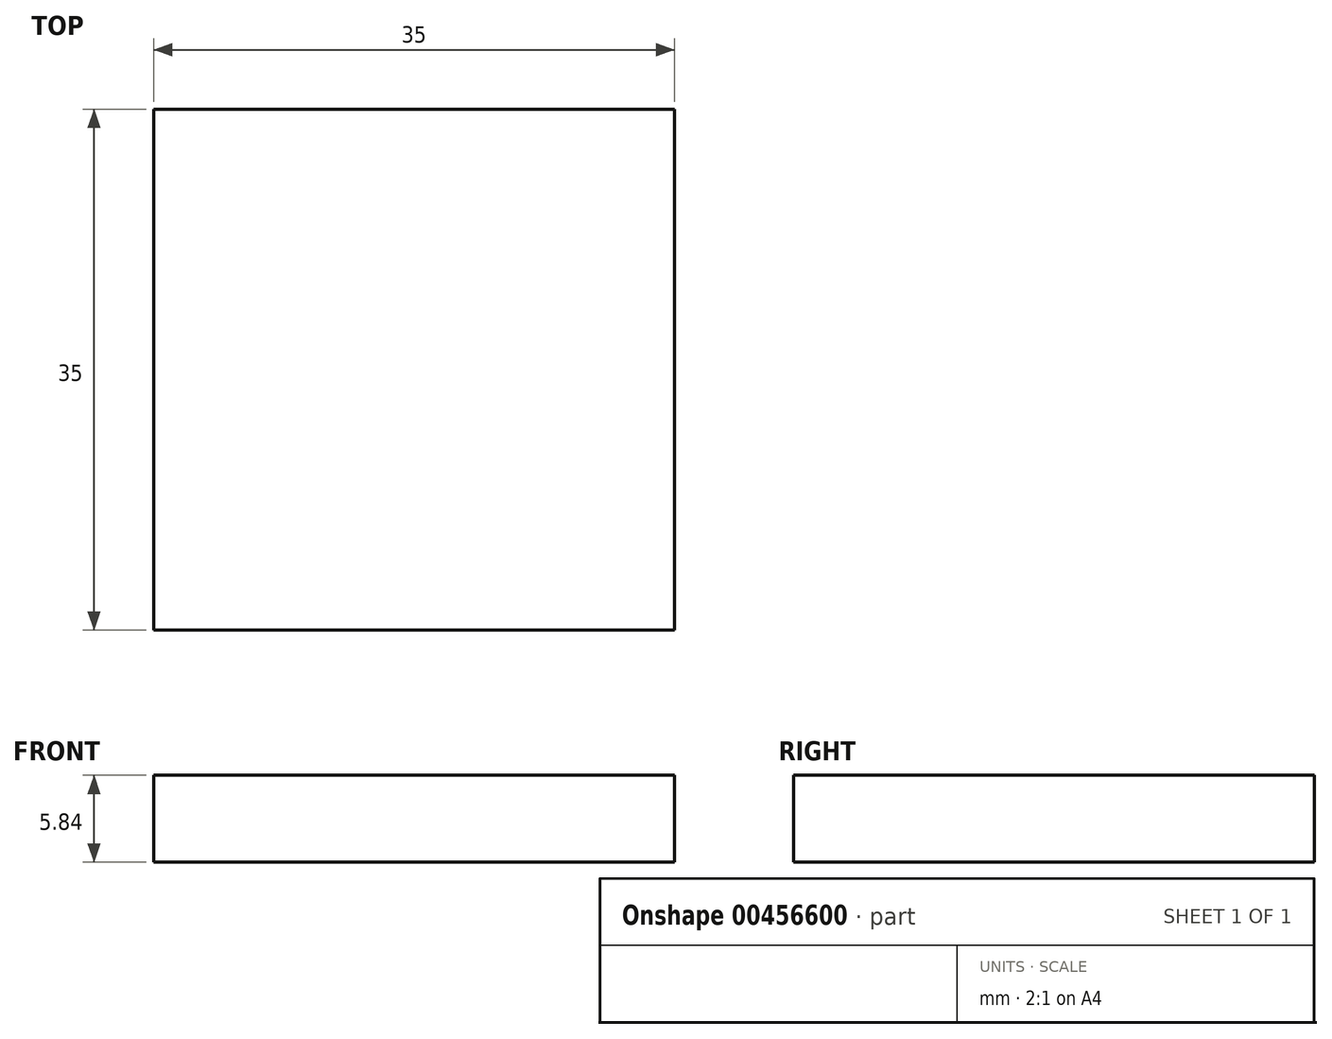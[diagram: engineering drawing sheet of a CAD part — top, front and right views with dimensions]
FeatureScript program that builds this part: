
annotation { "Feature Type Name" : "Feature", "Feature Type Description" : "" }
export const myFeature = defineFeature(function(context is Context, id is Id, definition is map)
    precondition{}
    {
        {
            var Q0;
            Q0=qCreatedBy(makeId("Top.planeOp"),FACE);
            var sketch = newSketch(context, id + "F0", { "sketchPlane" : qUnion([Q0])});
            skLineSegment(sketch, "E0.bottom", {"start": v(17.5, 17.5) * mm, "end": v(-17.5, 17.5) * mm});
            skLineSegment(sketch, "E0.top", {"start": v(17.5, -17.5) * mm, "end": v(-17.5, -17.5) * mm});
            skLineSegment(sketch, "E0.left", {"start": v(17.5, 17.5) * mm, "end": v(17.5, -17.5) * mm});
            skLineSegment(sketch, "E0.right", {"start": v(-17.5, 17.5) * mm, "end": v(-17.5, -17.5) * mm});
            skPoint(sketch, "E0.middle", {"position": v(0, 0) * mm});
            skSolve(sketch);
        }
        {
            var Q0;
            Q0=makeQuery(id+"F0.imprint","IMPRINT",FACE,{"disambiguationData":[TD([[makeQuery(id+"F0.imprint","IMPRINT",EDGE,{"derivedFrom":sQuery(id+"F0.wireOp",EDGE,"E0.bottom")}),1.0]])]});
            extrude(context, id + "F1", {"entities" : qUnion([Q0]), "depth" : 5.84 * mm});
        }
    });
